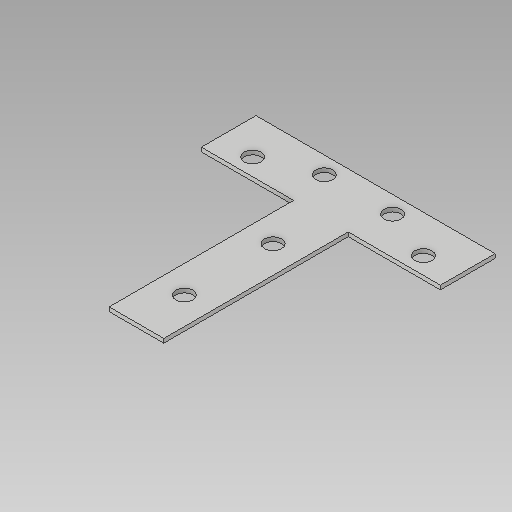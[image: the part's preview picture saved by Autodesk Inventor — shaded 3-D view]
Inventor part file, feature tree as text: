
AUTODESK INVENTOR PART (.ipt)
format: ipt  version: 2017 (Build 210142000, 142)  size: 113,152 bytes
history: native  units: in
note: dims shown in document units (in); Inventor stores cm internally (conversion verified against a paired STEP export)
features: extrude x1, sketch x1
ambient origin geometry x8: Origin, YZ Plane, XZ Plane, XY Plane, X Axis, Y Axis, Z Axis, Center Point
bodies: Solid1 (feature_tree)
feature tree (2):
  extrude  "Extrusion1"  Depth=0.6299in
  sketch  "Sketch1"  dims[d0=2.7559in d1=0.6299in d2=0.6299in d4=2.7559in d5=0.1969in d6=0.1969in d7=0.1969in d8=0.3937in d10=0.3937in d11=0.3937in d12=0.3937in d13=0.5512in d14=1.5748in d15=0.0472in d16=0.0in]
